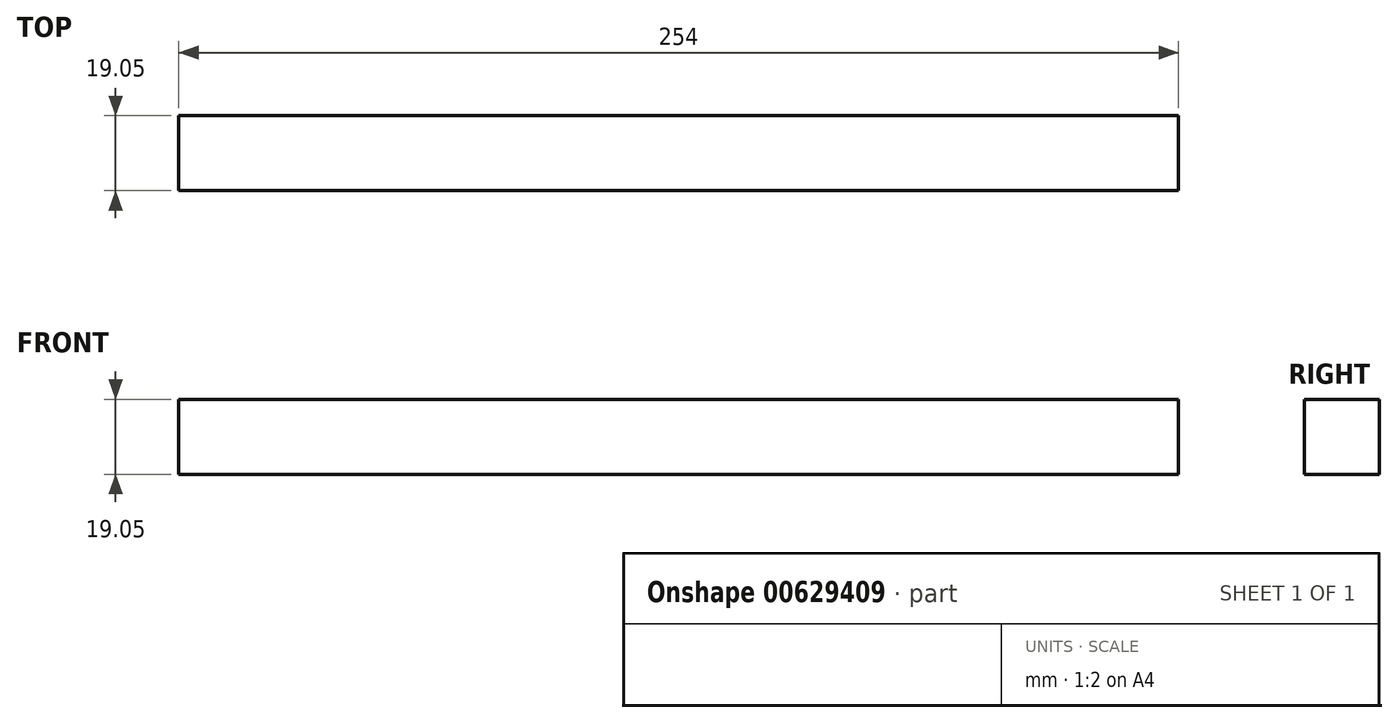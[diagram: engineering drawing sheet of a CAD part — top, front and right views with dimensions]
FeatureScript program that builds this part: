
annotation { "Feature Type Name" : "Feature", "Feature Type Description" : "" }
export const myFeature = defineFeature(function(context is Context, id is Id, definition is map)
    precondition{}
    {
        {
            var Q0;
            Q0=qCreatedBy(makeId("Front.planeOp"),FACE);
            var sketch = newSketch(context, id + "F0", { "sketchPlane" : qUnion([Q0])});
            skLineSegment(sketch, "E0.bottom", {"start": v(0, 0) * mm, "end": v(254, 0) * mm});
            skLineSegment(sketch, "E0.top", {"start": v(0, 19.05) * mm, "end": v(254, 19.05) * mm});
            skLineSegment(sketch, "E0.left", {"start": v(0, 0) * mm, "end": v(0, 19.05) * mm});
            skLineSegment(sketch, "E0.right", {"start": v(254, 0) * mm, "end": v(254, 19.05) * mm});
            skSolve(sketch);
        }
        {
            var Q0;
            Q0=qSketchRegion(id+"F0",true);
            extrude(context, id + "F1", {"entities" : qUnion([Q0]), "depth" : 19.05 * mm, "offsetDistance" : 25.4 * mm});
        }
    });
